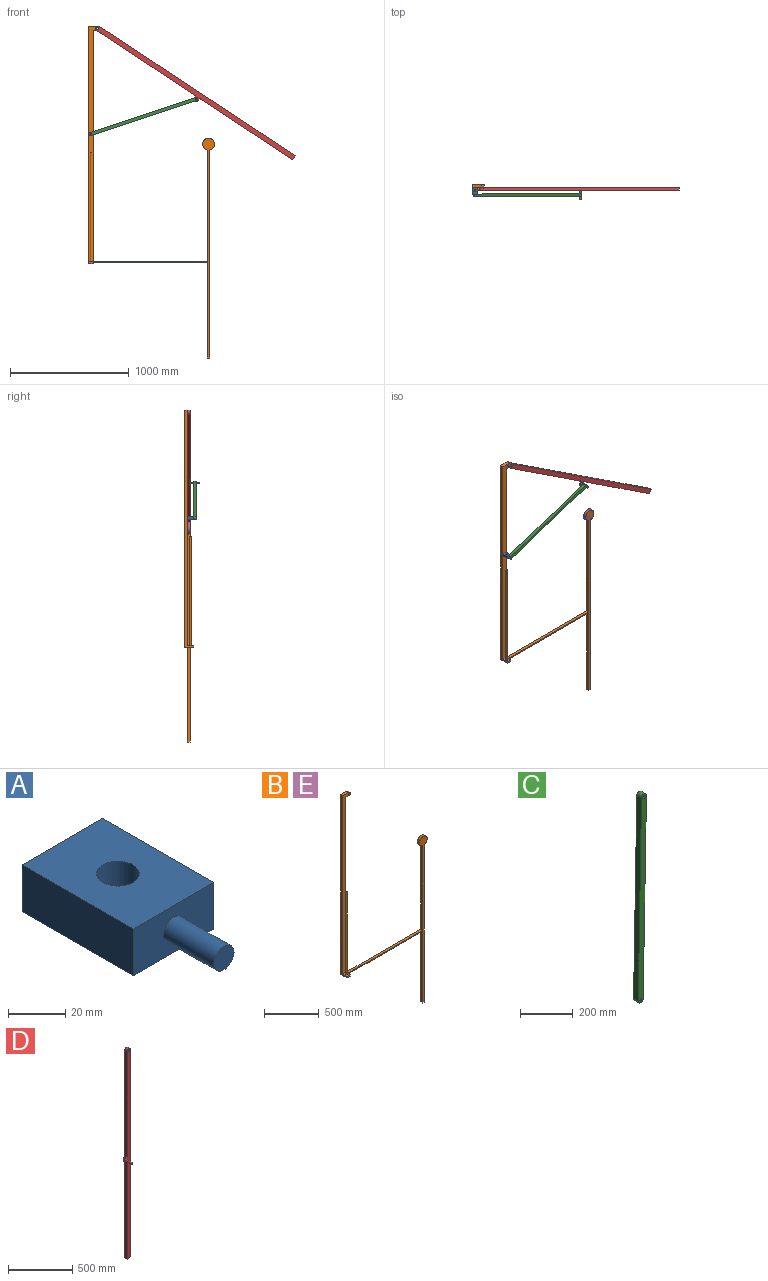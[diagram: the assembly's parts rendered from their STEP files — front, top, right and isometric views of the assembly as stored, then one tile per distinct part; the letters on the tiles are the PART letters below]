
ASSEMBLY  parts=5 mates=4
PART A: 9 faces, bbox 40x80x20 mm
  f0: plane 40x20mm, normal (0,1,0), area 800mm2, adj f1,f4,f5,f6
  f1: plane 55x20mm, normal (-1,0,0), area 1100mm2, adj f0,f2,f5,f6
  f2: plane 40x20mm, normal (0,-1,0), area 721.5mm2, adj f1,f4,f5,f6,f7
  f3: cylinder r=7.5mm len=20mm, axis (0,0,-1), area 942.5mm2, adj f5,f6
  f4: plane 55x20mm, normal (1,0,0), area 1100mm2, adj f0,f2,f5,f6
  f5: plane 55x40mm, normal (0,0,1), area 2023.3mm2, adj f0,f1,f2,f3,f4
  f6: plane 55x40mm, normal (0,0,-1), area 2023.3mm2, adj f0,f1,f2,f3,f4
  f7: cylinder r=5mm len=25mm, axis (0,1,0), area 785.4mm2, adj f2,f8
  f8: plane 10x10mm, normal (0,-1,0), area 78.5mm2, adj f7
PART B: 21 faces, bbox 1060x80x2795 mm
  f0: plane 1960x80mm, normal (1,0,0), area 49575mm2, adj f1,f5,f7,f8,f9,f10,f16,f19
  f1: plane 37.5x25mm, normal (0,0,-1), area 937.5mm2, adj f0,f2,f7,f8
  f2: cylinder r=20mm len=40mm, axis (0,1,0), area 1570.8mm2, adj f1,f3,f7,f8
  f3: plane 77.5x25mm, normal (0,0,1), area 1937.5mm2, adj f2,f4,f7,f8
  f4: plane 2000x80mm, normal (-1,0,0), area 50825mm2, adj f3,f5,f7,f8,f9,f10
  f5: plane 80x40mm, normal (0,0,-1), area 3200mm2, adj f0,f4,f8,f10
  f6: cylinder r=10mm len=25mm, axis (0,1,0), area 1570.8mm2, adj f7,f8
  f7: plane 1985x97.5mm, normal (0,-1,0), area 81214.2mm2, adj f0,f1,f2,f3,f4,f6,f9
  f8: plane 2000x97.5mm, normal (0,1,0), area 81814.2mm2, adj f0,f1,f2,f3,f4,f5,f6
  f9: plane 1000x55mm, normal (0,0,1), area 26023.3mm2, adj f0,f4,f7,f10,f11,f15,f19,f20
  f10: plane 40x15mm, normal (0,-1,0), area 600mm2, adj f0,f4,f5,f9
  f11: cylinder r=7.5mm len=919mm, axis (0,0,-1), area 43306.9mm2, adj f9,f12
  f12: plane 15x15mm, normal (0,0,1), area 176.7mm2, adj f11
  f13: plane 1751.01x25mm, normal (1,0,0), area 43775.3mm2, adj f14,f18,f19,f20
  f14: cylinder r=50mm len=100mm, axis (0,1,0), area 7350.6mm2, adj f13,f15,f19,f20
  f15: plane 941.01x25mm, normal (-1,0,0), area 23525.3mm2, adj f9,f14,f19,f20
  f16: plane 960x25mm, normal (0,0,-1), area 24000mm2, adj f0,f17,f19,f20
  f17: plane 800x25mm, normal (-1,0,0), area 20000mm2, adj f16,f18,f19,f20
  f18: plane 25x20mm, normal (0,0,-1), area 500mm2, adj f13,f17,f19,f20
  f19: plane 1850x1020mm, normal (0,-1,0), area 52460.7mm2, adj f0,f9,f13,f14,f15,f16,f17,f18
  f20: plane 1850x1020mm, normal (0,1,0), area 52460.7mm2, adj f0,f9,f13,f14,f15,f16,f17,f18
PART C: 8 faces, bbox 44x25x961.5 mm
  f0: plane 935x25mm, normal (1,0,-0.02), area 23379.1mm2, adj f1,f4,f6,f7
  f1: cylinder r=13.24mm len=26.49mm, axis (0,1,0), area 1040.2mm2, adj f0,f2,f6,f7
  f2: plane 935x25mm, normal (-1,0,0.02), area 23379.1mm2, adj f1,f4,f6,f7
  f3: cylinder r=7.5mm len=25mm, axis (0,1,0), area 1178.1mm2, adj f6,f7
  f4: cylinder r=13.24mm len=26.49mm, axis (0,1,0), area 1040.2mm2, adj f0,f2,f6,f7
  f5: cylinder r=5mm len=25mm, axis (0,1,0), area 785.4mm2, adj f6,f7
  f6: plane 961.49x43.99mm, normal (0,-1,0), area 25066.8mm2, adj f0,f1,f2,f3,f4,f5
  f7: plane 961.49x43.99mm, normal (0,1,0), area 25066.8mm2, adj f0,f1,f2,f3,f4,f5
PART D: 13 faces, bbox 80x103.3x2000 mm
  f0: plane 2000x80mm, normal (0,-1,0), area 80765.8mm2, adj f2,f3,f4,f5,f6,f8,f9,f10
  f1: plane 40x40mm, normal (0,1,0), area 1428.3mm2, adj f3,f8,f9,f10
  f2: cylinder r=20mm len=40mm, axis (0,1,0), area 1570.8mm2, adj f0,f3,f5,f7
  f3: plane 1980x25mm, normal (-1,0,0), area 49340mm2, adj f0,f1,f2,f4,f7,f8,f9
  f4: plane 40x25mm, normal (0,0,-1), area 1000mm2, adj f0,f3,f5,f7
  f5: plane 1980x25mm, normal (1,0,0), area 49500mm2, adj f0,f2,f4,f7
  f6: cylinder r=10mm len=25mm, axis (0,1,0), area 1570.8mm2, adj f0,f7
  f7: plane 2000x40mm, normal (0,1,0), area 79514.2mm2, adj f2,f3,f4,f5,f6
  f8: plane 20x4mm, normal (0,0,-1), area 80mm2, adj f0,f1,f3,f10
  f9: plane 20x4mm, normal (0,0,1), area 80mm2, adj f0,f1,f3,f10
  f10: cylinder r=20mm len=40mm, axis (0,-1,0), area 251.3mm2, adj f0,f1,f8,f9
  f11: cylinder r=7.5mm len=78.3mm, axis (0,1,0), area 3689.8mm2, adj f0,f12
  f12: plane 15x15mm, normal (0,-1,0), area 176.7mm2, adj f11
PART E: same geometry as B
PLACE A t=(0,0,1065.09)mm
PLACE B at identity fixed
PLACE C rot(axis=(0,1,0),70.5deg) t=(919.16,0,415.32)mm
PLACE D rot(axis=(0,-1,0),56.6deg) t=(844.25,0,392.87)mm
PLACE E at identity
MATE cylindrical C.f1 <-> D.f10  axis (0,1,0) through (887.28,-105,385.48)mm
MATE slider A.f3 <-> B.f11  axis (0,0,1) through (0,-52.5,100.09)mm
MATE revolute C.f4 <-> A.f7  axis (0,-1,0) through (0,-105,90.09)mm
MATE revolute B.f2 <-> D.f2  axis (0,-1,0) through (57.5,-25,980)mm
